FCSTD DOCUMENT  (FreeCAD 0.16RUnknown)
Label: calibpattern_coneLars
License: All rights reserved
LicenseURL: http://en.wikipedia.org/wiki/All_rights_reserved
objects: Sketcher::SketchObject×1, Spreadsheet::Sheet×1
note: 1 computed .brp shape members not serialized (recipe doc carries the construction recipe); baked Part::Feature solids carry a one-line shape summary decoded from their .brp

FEATURE [Sketcher::SketchObject] Sketch
  expr: Constraints[38] = Data.s_small + 3 * (Data.s_big - Data.s_small) / 4
  expr: Constraints[37] = Data.s_small + 2 * (Data.s_big - Data.s_small) / 4
  expr: Constraints[11] = Data.s_small
  expr: Constraints[36] = Data.s_small + (Data.s_big - Data.s_small) / 4
  expr: Constraints[24] = 3 * Data.alpha / 6
  expr: Constraints[7] = Data.alpha
  expr: Constraints[26] = 5 * Data.alpha / 6
  expr: Constraints[6] = Data.s_big
  expr: Constraints[25] = 4 * Data.alpha / 6
  expr: Constraints[22] = Data.alpha / 6
  expr: Constraints[23] = 2 * Data.alpha / 6
  sketch-geometry (12):
    g0: LineSegment StartX=0 StartY=0 StartZ=0 EndX=0 EndY=125.3 EndZ=0
    g1: ArcOfCircle CenterX=0 CenterY=0 CenterZ=0 NormalX=0 NormalY=0 NormalZ=1 Radius=125.3 StartAngle=1.5708 EndAngle=4.57951
    g2: LineSegment StartX=0 StartY=0 StartZ=0 EndX=-16.6004 EndY=-124.195 EndZ=0
    g3: ArcOfCircle CenterX=0 CenterY=0 CenterZ=0 NormalX=0 NormalY=0 NormalZ=1 Radius=27.1483 StartAngle=1.5708 EndAngle=4.57951
    g4: LineSegment StartX=0 StartY=0 StartZ=0 EndX=-74.2572 EndY=-100.925 EndZ=0
    g5: LineSegment StartX=0 StartY=0 StartZ=0 EndX=-113.63 EndY=-52.8043 EndZ=0
    g6: LineSegment StartX=0 StartY=0 StartZ=0 EndX=-125.023 EndY=8.31853 EndZ=0
    g7: LineSegment StartX=0 StartY=0 StartZ=0 EndX=-105.632 EndY=67.393 EndZ=0
    g8: LineSegment StartX=0 StartY=0 StartZ=0 EndX=-60.2315 EndY=109.873 EndZ=0
    g9: ArcOfCircle CenterX=0 CenterY=0 CenterZ=0 NormalX=0 NormalY=0 NormalZ=1 Radius=76.2239 StartAngle=1.5708 EndAngle=4.57951
    g10: ArcOfCircle CenterX=0 CenterY=0 CenterZ=0 NormalX=0 NormalY=0 NormalZ=1 Radius=100.762 StartAngle=1.5708 EndAngle=4.57951
    g11: ArcOfCircle CenterX=0 CenterY=0 CenterZ=0 NormalX=0 NormalY=0 NormalZ=1 Radius=51.6861 StartAngle=1.5708 EndAngle=4.57951
  constraints (39):
    c: Coincident(g0,g-1)
    c: PointOnObject(g0,g-2)
    c: Coincident(g1,g-1)
    c: Coincident(g1,g0)
    c: Coincident(g2,g-1)
    c: Coincident(g2,g1)
    c: Distance(g0) = 125.3
    c: Angle(g1) = 3.00872
    c: Coincident(g3,g-1)
    c: PointOnObject(g3,g0)
    c: PointOnObject(g3,g2)
    c: Radius(g3) = 27.1483
    c: Coincident(g4,g-1)
    c: Coincident(g5,g-1)
    c: PointOnObject(g5,g1)
    c: Coincident(g6,g-1)
    c: Coincident(g7,g-1)
    c: PointOnObject(g7,g1)
    c: PointOnObject(g8,g1)
    c: Coincident(g8,g-1)
    c: PointOnObject(g4,g1)
    c: PointOnObject(g6,g1)
    c: Angle(g4,g2) = 0.501453
    c: Angle(g5,g2) = 1.00291
    c: Angle(g6,g2) = 1.50436
    c: Angle(g7,g2) = 2.00581
    c: Angle(g8,g2) = 2.50726
    c: Coincident(g9,g-1)
    c: PointOnObject(g9,g0)
    c: PointOnObject(g9,g2)
    c: Coincident(g10,g-1)
    c: PointOnObject(g10,g0)
    c: PointOnObject(g10,g2)
    c: Coincident(g11,g-1)
    c: PointOnObject(g11,g0)
    c: PointOnObject(g11,g2)
    c: Radius(g11) = 51.6861
    c: Radius(g9) = 76.2239
    c: Radius(g10) = 100.762
FEATURE [Spreadsheet::Sheet] Spreadsheet  label="Data"
  cells = A1=R; B1(r_big)=60; A2=r; B2(r_small)=13; A3=H; B3(h_big)=110; A9=calculated:; A10=S; B10(s_big)==sqrt(h_big * h_big + r_big * r_big); C10=whole cone outer; A11=alpha; B11(alpha)==360 * r_big / s_big; A12=h; B12(h_small)==h_big * r_small / r_big; C12=top cone outer; A13=s; B13(s_small)==sqrt(h_small * h_small + r_small * r_small); C13=top cone outer
